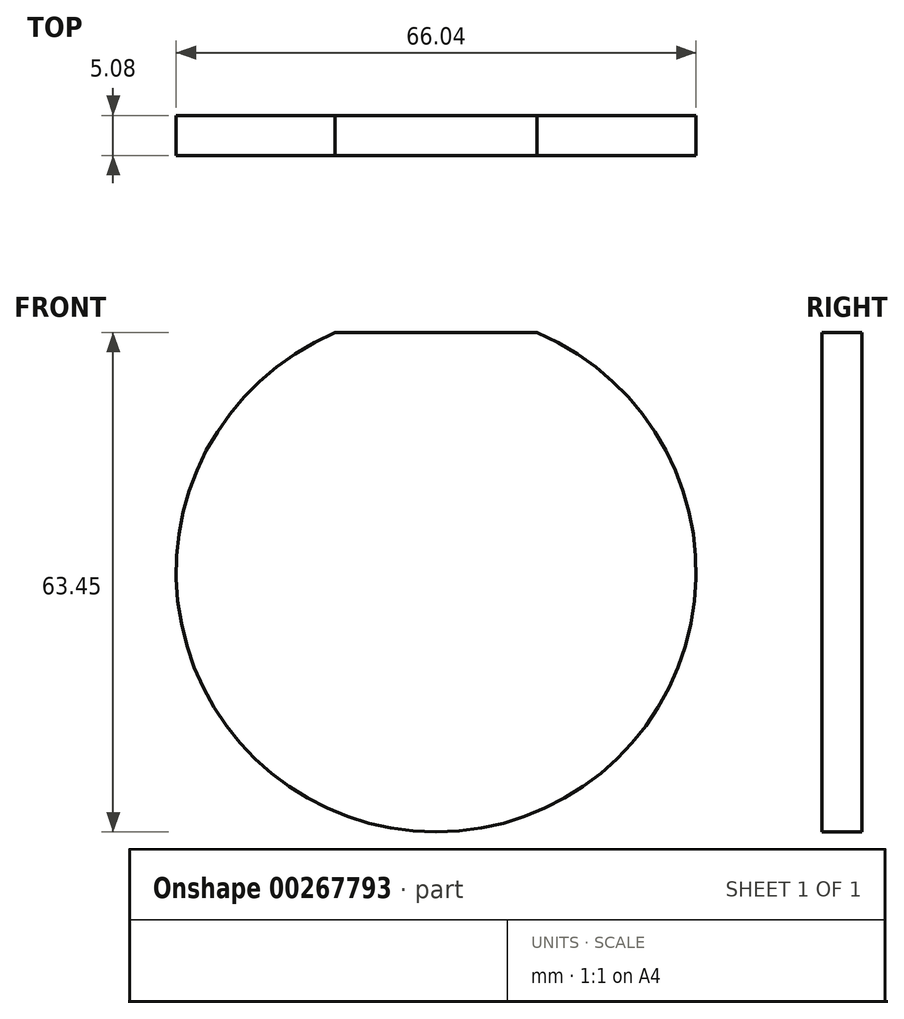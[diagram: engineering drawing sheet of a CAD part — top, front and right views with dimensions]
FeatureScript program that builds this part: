
annotation { "Feature Type Name" : "Feature", "Feature Type Description" : "" }
export const myFeature = defineFeature(function(context is Context, id is Id, definition is map)
    precondition{}
    {
        {
            var Q0;
            Q0=qCreatedBy(makeId("Front.planeOp"),FACE);
            var sketch = newSketch(context, id + "F0", { "sketchPlane" : qUnion([Q0])});
            skCircle(sketch, "E0", {"center": v(0, 0) * mm, "radius": 33.02 * mm});
            skLineSegment(sketch, "E1", {"start": v(-12.83, 30.43) * mm, "end": v(12.83, 30.43) * mm});
            skSolve(sketch);
        }
        {
            var Q0;
            {var subQ0=sQuery(id+"F0.wireOp",EDGE,"E1");Q0=makeQuery(id+"F0.imprint","IMPRINT",FACE,{"disambiguationData":[TD([[makeQuery(id+"F0.imprint","IMPRINT",EDGE,{"derivedFrom":subQ0}),-1.0]])]});}
            extrude(context, id + "F1", {"entities" : qUnion([Q0]), "depth" : 5.08 * mm});
        }
    });
